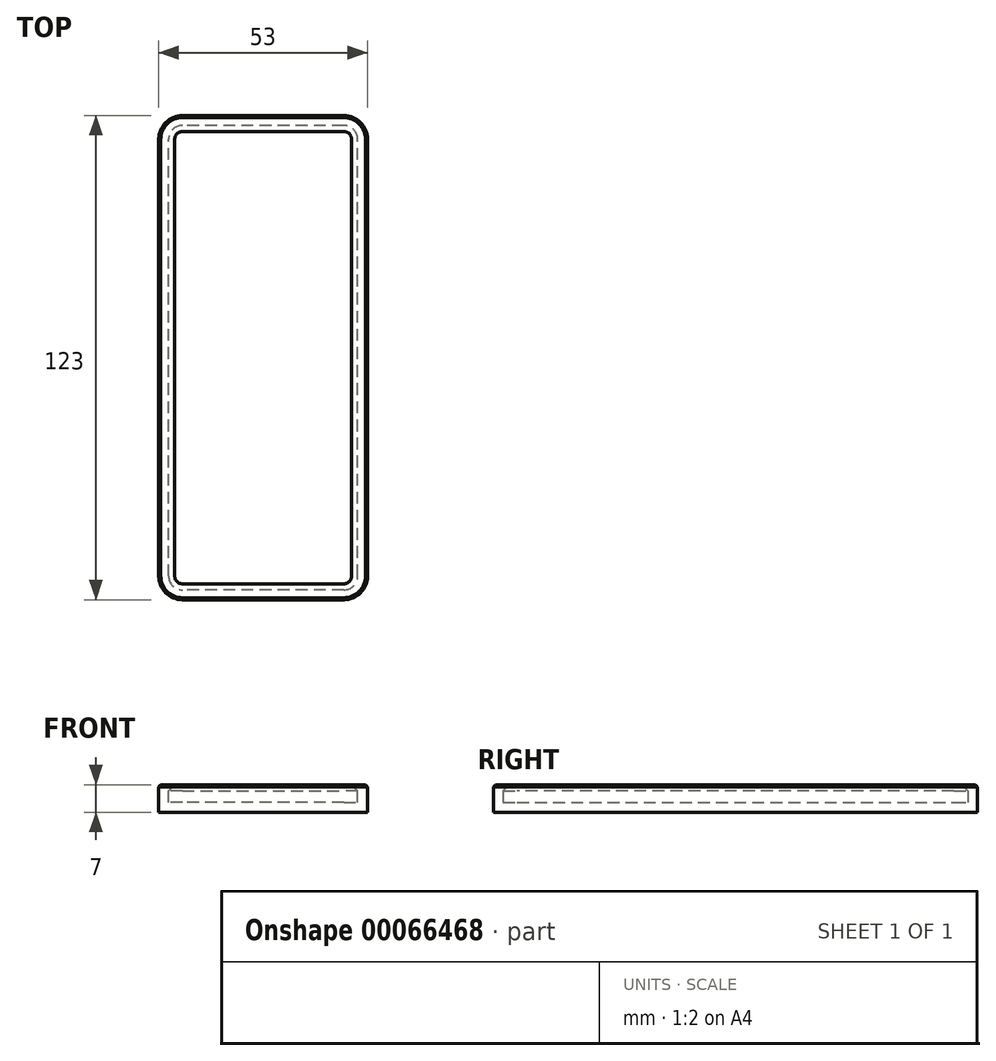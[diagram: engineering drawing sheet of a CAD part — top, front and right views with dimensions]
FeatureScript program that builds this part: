
annotation { "Feature Type Name" : "Feature", "Feature Type Description" : "" }
export const myFeature = defineFeature(function(context is Context, id is Id, definition is map)
    precondition{}
    {
        {
            var Q0;
            Q0=qCreatedBy(makeId("Top.planeOp"),FACE);
            var sketch = newSketch(context, id + "F0", { "sketchPlane" : qUnion([Q0])});
            skLineSegment(sketch, "E0.rect.bottom", {"start": v(26.5, -61.5) * mm, "end": v(-26.5, -61.5) * mm});
            skLineSegment(sketch, "E0.rect.top", {"start": v(26.5, 61.5) * mm, "end": v(-26.5, 61.5) * mm});
            skLineSegment(sketch, "E0.rect.left", {"start": v(26.5, -61.5) * mm, "end": v(26.5, 61.5) * mm});
            skLineSegment(sketch, "E0.rect.right", {"start": v(-26.5, -61.5) * mm, "end": v(-26.5, 61.5) * mm});
            skPoint(sketch, "E0.rect.middle", {"position": v(0, 0) * mm});
            skSolve(sketch);
        }
        {
            var Q0;
            Q0=makeQuery(id+"F0.imprint","IMPRINT",FACE,{"disambiguationData":[TD([[makeQuery(id+"F0.imprint","IMPRINT",EDGE,{"derivedFrom":sQuery(id+"F0.wireOp",EDGE,"E0.rect.bottom")}),-1.0]])]});
            extrude(context, id + "F1", {"entities" : qUnion([Q0]), "depth" : 7 * mm});
        }
        {
            var Q0;
            Q0=makeQuery(id+"F1.opExtrude","SWEPT_EDGE",EDGE,{"disambiguationData":[OSD([sQuery(id+"F0.wireOp",EDGE,"E0.rect.top"),sQuery(id+"F0.wireOp",EDGE,"E0.rect.left")])]});
            var Q1;
            Q1=makeQuery(id+"F1.opExtrude","SWEPT_EDGE",EDGE,{"disambiguationData":[OSD([sQuery(id+"F0.wireOp",EDGE,"E0.rect.top"),sQuery(id+"F0.wireOp",EDGE,"E0.rect.right")])]});
            var Q2;
            Q2=makeQuery(id+"F1.opExtrude","SWEPT_EDGE",EDGE,{"disambiguationData":[OSD([sQuery(id+"F0.wireOp",EDGE,"E0.rect.bottom"),sQuery(id+"F0.wireOp",EDGE,"E0.rect.left")])]});
            var Q3;
            Q3=makeQuery(id+"F1.opExtrude","SWEPT_EDGE",EDGE,{"disambiguationData":[OSD([sQuery(id+"F0.wireOp",EDGE,"E0.rect.bottom"),sQuery(id+"F0.wireOp",EDGE,"E0.rect.right")])]});
            fillet(context, id + "F2", {"entities" : qUnion([Q0, Q1, Q2, Q3]), "radius" : 6 * mm, "tangentPropagation" : true, "allowEdgeOverflow" : false});
        }
        {
            var Q0;
            Q0=makeQuery(id+"F1.opExtrude","CAP_EDGE",EDGE,{"disambiguationData":[OSD([sQuery(id+"F0.wireOp",EDGE,"E0.rect.right")])],"isStart":false});
            var Q1;
            {var subQ0=sQuery(id+"F0.wireOp",EDGE,"E0.rect.bottom");var subQ1=sQuery(id+"F0.wireOp",EDGE,"E0.rect.right");Q1=makeQuery(id+"F2.opFillet","BLEND_EDGE",EDGE,{"blendedFrom":[makeQuery(id+"F1.opExtrude","SWEPT_EDGE",EDGE,{"disambiguationData":[OSD([subQ0,subQ1])]}),makeQuery(id+"F1.opExtrude","CAP_FACE",FACE,{"disambiguationData":[OSD([subQ0,sQuery(id+"F0.wireOp",EDGE,"E0.rect.top"),sQuery(id+"F0.wireOp",EDGE,"E0.rect.left"),subQ1])],"isStart":false})],"blendedInto":[makeQuery(id+"F1.opExtrude","CAP_FACE",FACE,{"disambiguationData":[OSD([subQ0,sQuery(id+"F0.wireOp",EDGE,"E0.rect.top"),sQuery(id+"F0.wireOp",EDGE,"E0.rect.left"),subQ1])],"isStart":false})]});}
            var Q2;
            Q2=makeQuery(id+"F1.opExtrude","CAP_EDGE",EDGE,{"disambiguationData":[OSD([sQuery(id+"F0.wireOp",EDGE,"E0.rect.bottom")])],"isStart":false});
            var Q3;
            {var subQ0=sQuery(id+"F0.wireOp",EDGE,"E0.rect.bottom");var subQ1=sQuery(id+"F0.wireOp",EDGE,"E0.rect.left");Q3=makeQuery(id+"F2.opFillet","BLEND_EDGE",EDGE,{"blendedFrom":[makeQuery(id+"F1.opExtrude","SWEPT_EDGE",EDGE,{"disambiguationData":[OSD([subQ0,subQ1])]}),makeQuery(id+"F1.opExtrude","CAP_FACE",FACE,{"disambiguationData":[OSD([subQ0,sQuery(id+"F0.wireOp",EDGE,"E0.rect.top"),subQ1,sQuery(id+"F0.wireOp",EDGE,"E0.rect.right")])],"isStart":false})],"blendedInto":[makeQuery(id+"F1.opExtrude","CAP_FACE",FACE,{"disambiguationData":[OSD([subQ0,sQuery(id+"F0.wireOp",EDGE,"E0.rect.top"),subQ1,sQuery(id+"F0.wireOp",EDGE,"E0.rect.right")])],"isStart":false})]});}
            var Q4;
            Q4=makeQuery(id+"F1.opExtrude","CAP_EDGE",EDGE,{"disambiguationData":[OSD([sQuery(id+"F0.wireOp",EDGE,"E0.rect.left")])],"isStart":false});
            var Q5;
            {var subQ0=sQuery(id+"F0.wireOp",EDGE,"E0.rect.top");var subQ1=sQuery(id+"F0.wireOp",EDGE,"E0.rect.left");Q5=makeQuery(id+"F2.opFillet","BLEND_EDGE",EDGE,{"blendedFrom":[makeQuery(id+"F1.opExtrude","SWEPT_EDGE",EDGE,{"disambiguationData":[OSD([subQ0,subQ1])]}),makeQuery(id+"F1.opExtrude","CAP_FACE",FACE,{"disambiguationData":[OSD([sQuery(id+"F0.wireOp",EDGE,"E0.rect.bottom"),subQ0,subQ1,sQuery(id+"F0.wireOp",EDGE,"E0.rect.right")])],"isStart":false})],"blendedInto":[makeQuery(id+"F1.opExtrude","CAP_FACE",FACE,{"disambiguationData":[OSD([sQuery(id+"F0.wireOp",EDGE,"E0.rect.bottom"),subQ0,subQ1,sQuery(id+"F0.wireOp",EDGE,"E0.rect.right")])],"isStart":false})]});}
            var Q6;
            Q6=makeQuery(id+"F1.opExtrude","CAP_EDGE",EDGE,{"disambiguationData":[OSD([sQuery(id+"F0.wireOp",EDGE,"E0.rect.top")])],"isStart":false});
            var Q7;
            {var subQ0=sQuery(id+"F0.wireOp",EDGE,"E0.rect.top");var subQ1=sQuery(id+"F0.wireOp",EDGE,"E0.rect.right");Q7=makeQuery(id+"F2.opFillet","BLEND_EDGE",EDGE,{"blendedFrom":[makeQuery(id+"F1.opExtrude","SWEPT_EDGE",EDGE,{"disambiguationData":[OSD([subQ0,subQ1])]}),makeQuery(id+"F1.opExtrude","CAP_FACE",FACE,{"disambiguationData":[OSD([sQuery(id+"F0.wireOp",EDGE,"E0.rect.bottom"),subQ0,sQuery(id+"F0.wireOp",EDGE,"E0.rect.left"),subQ1])],"isStart":false})],"blendedInto":[makeQuery(id+"F1.opExtrude","CAP_FACE",FACE,{"disambiguationData":[OSD([sQuery(id+"F0.wireOp",EDGE,"E0.rect.bottom"),subQ0,sQuery(id+"F0.wireOp",EDGE,"E0.rect.left"),subQ1])],"isStart":false})]});}
            chamfer(context, id + "F3", {"entities" : qUnion([Q0, Q1, Q2, Q3, Q4, Q5, Q6, Q7]), "width" : 0.5 * mm, "tangentPropagation" : true});
        }
        {
            var Q0;
            Q0=makeQuery(id+"F1.opExtrude","CAP_FACE",FACE,{"disambiguationData":[OSD([sQuery(id+"F0.wireOp",EDGE,"E0.rect.bottom"),sQuery(id+"F0.wireOp",EDGE,"E0.rect.top"),sQuery(id+"F0.wireOp",EDGE,"E0.rect.left"),sQuery(id+"F0.wireOp",EDGE,"E0.rect.right")])],"isStart":false});
            shell(context, id + "F4", {"entities" : qUnion([Q0]), "thickness" : 2.5 * mm});
        }
    });
